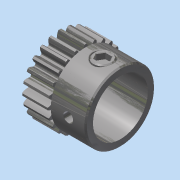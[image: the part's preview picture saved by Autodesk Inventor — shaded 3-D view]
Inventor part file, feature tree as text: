
AUTODESK INVENTOR PART (.ipt)
format: ipt  version: 2015 (Build 190159000, 159)  size: 1,200,640 bytes
history: native  units: in
note: dims shown in document units (in); Inventor stores cm internally (conversion verified against a paired STEP export)
features: imported_body x2, other x1, extrude x1, sketch x1
ambient origin geometry x8: Origin, YZ Plane, XZ Plane, XY Plane, X Axis, Y Axis, Z Axis, Center Point
bodies: Solid1 (feature_tree), Solid2 (feature_tree)
feature tree (5):
  other  "s1086z-048s0241"
  extrude  "Extrusion1"  TaperAngle=0.0deg  [1 undecoded]
  imported_body  "Base1"
  imported_body  "Base2"
  sketch  "Sketch1"  dims[d0=0.3937in d1=0.0in d2=0.0in]
note: 1 required parameter value undecoded (feature->parameter linkage not recoverable at this tier; creation-order binding heuristic only, values carry confidence <= 0.55)
